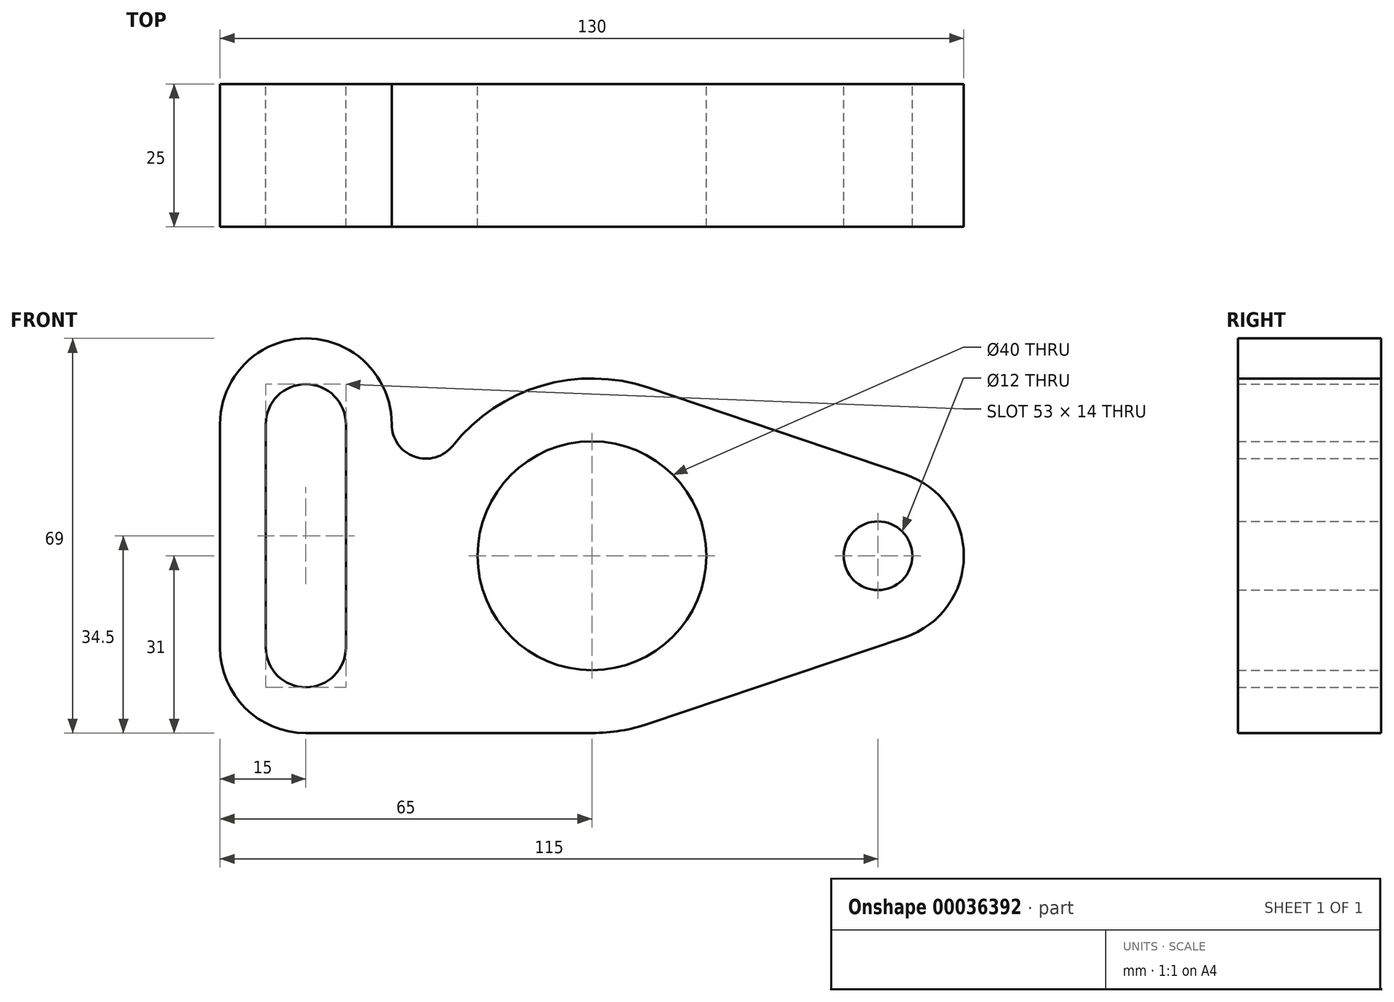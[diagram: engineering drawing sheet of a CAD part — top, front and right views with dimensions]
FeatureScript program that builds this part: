
annotation { "Feature Type Name" : "Feature", "Feature Type Description" : "" }
export const myFeature = defineFeature(function(context is Context, id is Id, definition is map)
    precondition{}
    {
        {
            var Q0;
            Q0=qCreatedBy(makeId("Front.planeOp"),FACE);
            var sketch = newSketch(context, id + "F0", { "sketchPlane" : qUnion([Q0])});
            skArc(sketch, "E0", {"start": v(0, -31) * mm, "mid": v(5.03, -30.59) * mm, "end": v(9.92, -29.37) * mm});
            skCircle(sketch, "E1", {"center": v(0, 0) * mm, "radius": 20 * mm});
            skCircle(sketch, "E2", {"center": v(50, 0) * mm, "radius": 6 * mm});
            skArc(sketch, "E3", {"start": v(54.8, -14.21) * mm, "mid": v(65, 0) * mm, "end": v(54.8, 14.21) * mm});
            skArc(sketch, "E4", {"start": v(-35, 22.98) * mm, "mid": v(-50, 38) * mm, "end": v(-65, 23) * mm});
            skArc(sketch, "E5", {"start": v(-43, 23) * mm, "mid": v(-50, 30) * mm, "end": v(-57, 23) * mm});
            skArc(sketch, "E6", {"start": v(-65, -16) * mm, "mid": v(-60.6, -26.6) * mm, "end": v(-50, -31) * mm});
            skArc(sketch, "E7", {"start": v(-57, -16) * mm, "mid": v(-50, -23) * mm, "end": v(-43, -16) * mm});
            skArc(sketch, "E8", {"start": v(-35, 22.98) * mm, "mid": v(-30.98, 17.31) * mm, "end": v(-24.3, 19.25) * mm});
            skLineSegment(sketch, "E9", {"start": v(-50, -16) * mm, "end": v(-50, 23) * mm, "construction": true});
            skLineSegment(sketch, "E10", {"start": v(-65, 23) * mm, "end": v(-65, -16) * mm});
            skLineSegment(sketch, "E11", {"start": v(-50, -31) * mm, "end": v(0, -31) * mm});
            skLineSegment(sketch, "E12", {"start": v(9.92, -29.37) * mm, "end": v(54.8, -14.21) * mm});
            skLineSegment(sketch, "E13", {"start": v(54.8, 14.21) * mm, "end": v(9.92, 29.37) * mm});
            skLineSegment(sketch, "E14", {"start": v(-57, 23) * mm, "end": v(-57, -16) * mm});
            skLineSegment(sketch, "E15", {"start": v(-43, 23) * mm, "end": v(-43, -16) * mm});
            skArc(sketch, "E16.trimOffspring", {"start": v(9.92, 29.37) * mm, "mid": v(-8.8, 29.73) * mm, "end": v(-24.3, 19.25) * mm});
            skSolve(sketch);
        }
        {
            var Q0;
            Q0=makeQuery(id+"F0.imprint","IMPRINT",FACE,{"disambiguationData":[TD([[makeQuery(id+"F0.imprint","IMPRINT",EDGE,{"derivedFrom":sQuery(id+"F0.wireOp",EDGE,"E0")}),1.0]])]});
            extrude(context, id + "F1", {"entities" : qUnion([Q0]), "depth" : 25 * mm});
        }
    });
